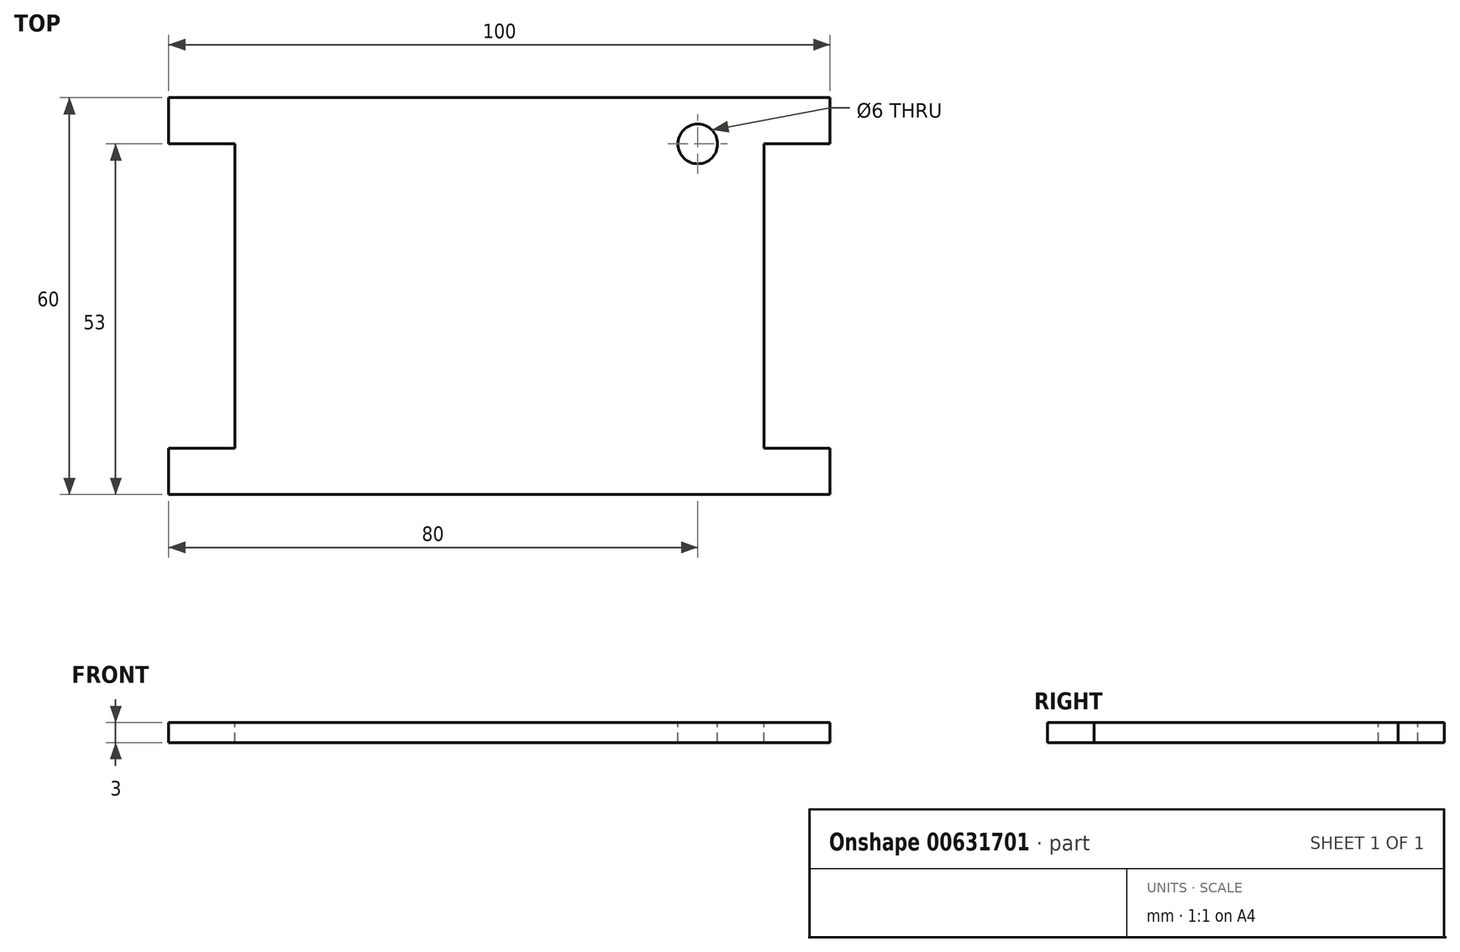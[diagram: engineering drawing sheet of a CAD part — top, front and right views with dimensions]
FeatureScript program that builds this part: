
annotation { "Feature Type Name" : "Feature", "Feature Type Description" : "" }
export const myFeature = defineFeature(function(context is Context, id is Id, definition is map)
    precondition{}
    {
        {
            var Q0;
            Q0=qCreatedBy(makeId("Top.planeOp"),FACE);
            var sketch = newSketch(context, id + "F0", { "sketchPlane" : qUnion([Q0])});
            skLineSegment(sketch, "E0.bottom", {"start": v(50, -30) * mm, "end": v(-50, -30) * mm});
            skLineSegment(sketch, "E0.top", {"start": v(50, 30) * mm, "end": v(-50, 30) * mm});
            skLineSegment(sketch, "E0.left", {"start": v(50, -30) * mm, "end": v(50, 30) * mm});
            skLineSegment(sketch, "E0.right", {"start": v(-50, -30) * mm, "end": v(-50, 30) * mm});
            skPoint(sketch, "E0.middle", {"position": v(0, 0) * mm});
            skSolve(sketch);
        }
        {
            var Q0;
            Q0 = qSketchRegion(id + "F0", true);
            extrude(context, id + "F1", {"entities" : qUnion([Q0]), "depth" : 3 * mm, "offsetDistance" : 25 * mm});
        }
        {
            var Q0;
            Q0=makeQuery(id+"F1.opExtrude","CAP_FACE",FACE,{"disambiguationData":[OSD([sQuery(id+"F0.wireOp",EDGE,"E0.bottom"),sQuery(id+"F0.wireOp",EDGE,"E0.top"),sQuery(id+"F0.wireOp",EDGE,"E0.left"),sQuery(id+"F0.wireOp",EDGE,"E0.right")])],"isStart":false});
            var sketch = newSketch(context, id + "F2", { "sketchPlane" : qUnion([Q0])});
            skLineSegment(sketch, "E1", {"start": v(0, 0) * mm, "end": v(-50, 0) * mm});
            skLineSegment(sketch, "E2", {"start": v(0, 0) * mm, "end": v(50, 0) * mm});
            skPoint(sketch, "E3", {"position": v(-50, 23) * mm});
            skPoint(sketch, "E4", {"position": v(-50, -23) * mm});
            skPoint(sketch, "E5", {"position": v(50, -23) * mm});
            skPoint(sketch, "E6", {"position": v(50, 23) * mm});
            skPoint(sketch, "E7", {"position": v(-40, 0) * mm});
            skPoint(sketch, "E8", {"position": v(40, 0) * mm});
            skPoint(sketch, "E9", {"position": v(-40, 23) * mm});
            skPoint(sketch, "E10", {"position": v(-40, -23) * mm});
            skPoint(sketch, "E11", {"position": v(40, -23) * mm});
            skPoint(sketch, "E12", {"position": v(40, 23) * mm});
            skLineSegment(sketch, "E13", {"start": v(-50, 23) * mm, "end": v(-40, 23) * mm});
            skLineSegment(sketch, "E14", {"start": v(-40, 0) * mm, "end": v(-40, 23) * mm});
            skLineSegment(sketch, "E15", {"start": v(-50, -23) * mm, "end": v(-40, -23) * mm});
            skLineSegment(sketch, "E16", {"start": v(-40, -23) * mm, "end": v(-40, 0) * mm});
            skLineSegment(sketch, "E17", {"start": v(50, 23) * mm, "end": v(40, 23) * mm});
            skLineSegment(sketch, "E18", {"start": v(40, 23) * mm, "end": v(40, 0) * mm});
            skLineSegment(sketch, "E19", {"start": v(50, -23) * mm, "end": v(40, -23) * mm});
            skLineSegment(sketch, "E20", {"start": v(40, -23) * mm, "end": v(40, 0) * mm});
            skSolve(sketch);
        }
        {
            var Q0;
            {var subQ4=sQuery(id+"F2.wireOp",EDGE,"E13");Q0=makeQuery(id+"F2.imprint","IMPRINT",FACE,{"disambiguationData":[TD([[makeQuery(id+"F2.imprint","IMPRINT",EDGE,{"derivedFrom":subQ4}),-1.0]])]});}
            var Q1;
            {var subQ4=sQuery(id+"F2.wireOp",EDGE,"E15");Q1=makeQuery(id+"F2.imprint","IMPRINT",FACE,{"disambiguationData":[TD([[makeQuery(id+"F2.imprint","IMPRINT",EDGE,{"derivedFrom":subQ4}),1.0]])]});}
            var Q2;
            {var subQ4=sQuery(id+"F2.wireOp",EDGE,"E17");Q2=makeQuery(id+"F2.imprint","IMPRINT",FACE,{"disambiguationData":[TD([[makeQuery(id+"F2.imprint","IMPRINT",EDGE,{"derivedFrom":subQ4}),1.0]])]});}
            var Q3;
            {var subQ4=sQuery(id+"F2.wireOp",EDGE,"E19");Q3=makeQuery(id+"F2.imprint","IMPRINT",FACE,{"disambiguationData":[TD([[makeQuery(id+"F2.imprint","IMPRINT",EDGE,{"derivedFrom":subQ4}),-1.0]])]});}
            extrude(context, id + "F3", {"entities" : qUnion([Q0, Q1, Q2, Q3]), "operationType" : NewBodyOperationType.REMOVE, "endBound" : BoundingType.THROUGH_ALL, "oppositeDirection" : true, "depth" : 25 * mm, "offsetDistance" : 25 * mm});
        }
        {
            var Q0;
            Q0=makeQuery(id+"F1.opExtrude","CAP_FACE",FACE,{"disambiguationData":[OSD([sQuery(id+"F0.wireOp",EDGE,"E0.bottom"),sQuery(id+"F0.wireOp",EDGE,"E0.top"),sQuery(id+"F0.wireOp",EDGE,"E0.left"),sQuery(id+"F0.wireOp",EDGE,"E0.right")])],"isStart":false});
            var sketch = newSketch(context, id + "F4", { "sketchPlane" : qUnion([Q0])});
            skPoint(sketch, "E21", {"position": v(30, 23) * mm});
            skCircle(sketch, "E22", {"center": v(30, 23) * mm, "radius": 3 * mm});
            skSolve(sketch);
        }
        {
            var Q0;
            Q0=makeQuery(id+"F4.imprint","IMPRINT",FACE,{"disambiguationData":[TD([[makeQuery(id+"F4.imprint","IMPRINT",EDGE,{"derivedFrom":sQuery(id+"F4.wireOp",EDGE,"E22")}),1.0]])]});
            extrude(context, id + "F5", {"entities" : qUnion([Q0]), "operationType" : NewBodyOperationType.REMOVE, "endBound" : BoundingType.THROUGH_ALL, "oppositeDirection" : true, "depth" : 25 * mm, "offsetDistance" : 25 * mm});
        }
    });
